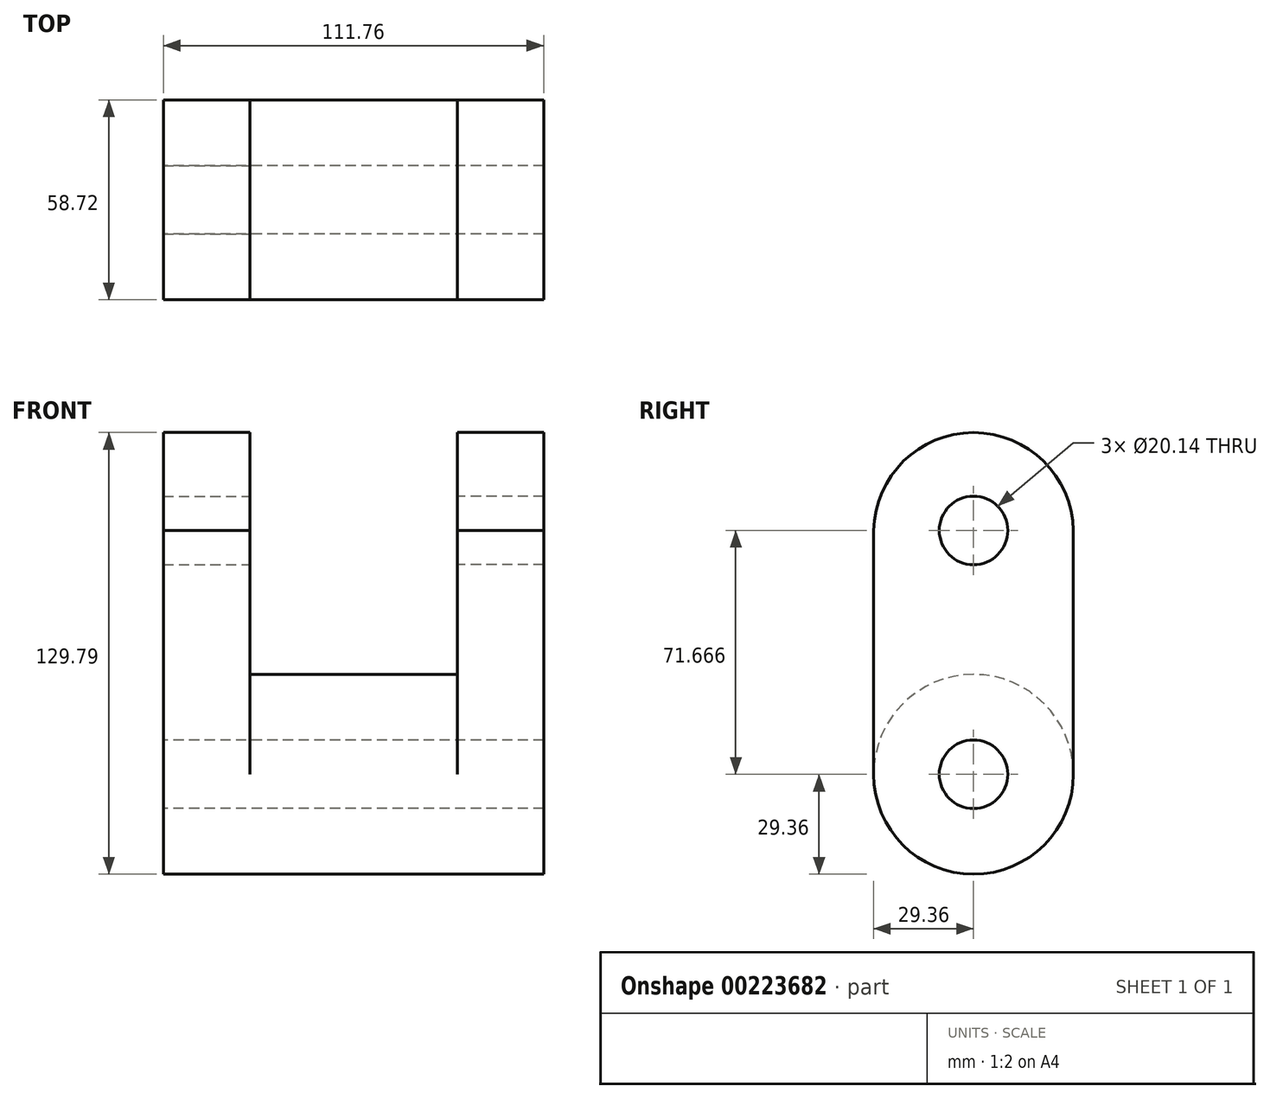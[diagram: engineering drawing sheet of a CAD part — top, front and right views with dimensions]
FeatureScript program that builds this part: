
annotation { "Feature Type Name" : "Feature", "Feature Type Description" : "" }
export const myFeature = defineFeature(function(context is Context, id is Id, definition is map)
    precondition{}
    {
        {
            var Q0;
            Q0=qCreatedBy(makeId("Right.planeOp"),FACE);
            var sketch = newSketch(context, id + "F0", { "sketchPlane" : qUnion([Q0])});
            skCircle(sketch, "E0", {"center": v(0, 0) * mm, "radius": 29.36 * mm});
            skLineSegment(sketch, "E1", {"start": v(-29.36, 0) * mm, "end": v(-29.36, 71.67) * mm});
            skLineSegment(sketch, "E2", {"start": v(-29.36, 71.67) * mm, "end": v(-29.35, 71.67) * mm});
            skLineSegment(sketch, "E3", {"start": v(29.36, 71.67) * mm, "end": v(29.36, 0) * mm});
            skArc(sketch, "E4", {"start": v(29.36, 71.07) * mm, "mid": v(0, 100.43) * mm, "end": v(-29.36, 71.07) * mm});
            skCircle(sketch, "E5", {"center": v(0, 0) * mm, "radius": 10.07 * mm});
            skCircle(sketch, "E6", {"center": v(0, 71.67) * mm, "radius": 10.07 * mm});
            skLineSegment(sketch, "E7.trimOffspring", {"start": v(29.35, 71.67) * mm, "end": v(29.36, 71.67) * mm});
            skSolve(sketch);
        }
        {
            var Q0;
            Q0 = qSketchRegion(id + "F0", true);
            extrude(context, id + "F1", {"entities" : qUnion([Q0]), "depth" : 25.4 * mm});
        }
        {
            var Q0;
            Q0=makeQuery(id+"F0.imprint","IMPRINT",FACE,{"disambiguationData":[TD([[makeQuery(id+"F0.imprint","IMPRINT",EDGE,{"derivedFrom":sQuery(id+"F0.wireOp",EDGE,"E5")}),-1.0]])]});
            extrude(context, id + "F2", {"entities" : qUnion([Q0]), "operationType" : NewBodyOperationType.ADD, "oppositeDirection" : true, "depth" : 30.48 * mm});
        }
        {
            var Q0;
            Q0=makeQuery(id+"F2.opExtrude","CAP_FACE",FACE,{"disambiguationData":[OSD([sQuery(id+"F0.wireOp",EDGE,"E0"),sQuery(id+"F0.wireOp",EDGE,"E5")])],"isStart":false});
            cPlane(context, id + "F3", {"entities" : qUnion([Q0]), "cplaneType" : CPlaneType.OFFSET, "offset" : 0 * mm, "width" : 152.4 * mm, "height" : 152.4 * mm});
        }
        {
            var Q0;
            Q0=makeQuery(id+"F1.opExtrude","SWEPT_BODY",BODY,{"disambiguationData":[OSD([sQuery(id+"F0.wireOp",EDGE,"E0"),sQuery(id+"F0.wireOp",EDGE,"E1"),sQuery(id+"F0.wireOp",EDGE,"E2"),sQuery(id+"F0.wireOp",EDGE,"E3"),sQuery(id+"F0.wireOp",EDGE,"E4"),sQuery(id+"F0.wireOp",EDGE,"E5"),sQuery(id+"F0.wireOp",EDGE,"E6"),sQuery(id+"F0.wireOp",EDGE,"E7.trimOffspring")])]});
            var Q1;
            Q1=qCreatedBy(id+"F3.planeOp",FACE);
            mirror(context, id + "F4", {"operationType" : NewBodyOperationType.ADD, "entities" : qUnion([Q0]), "mirrorPlane" : qUnion([Q1])});
        }
    });
